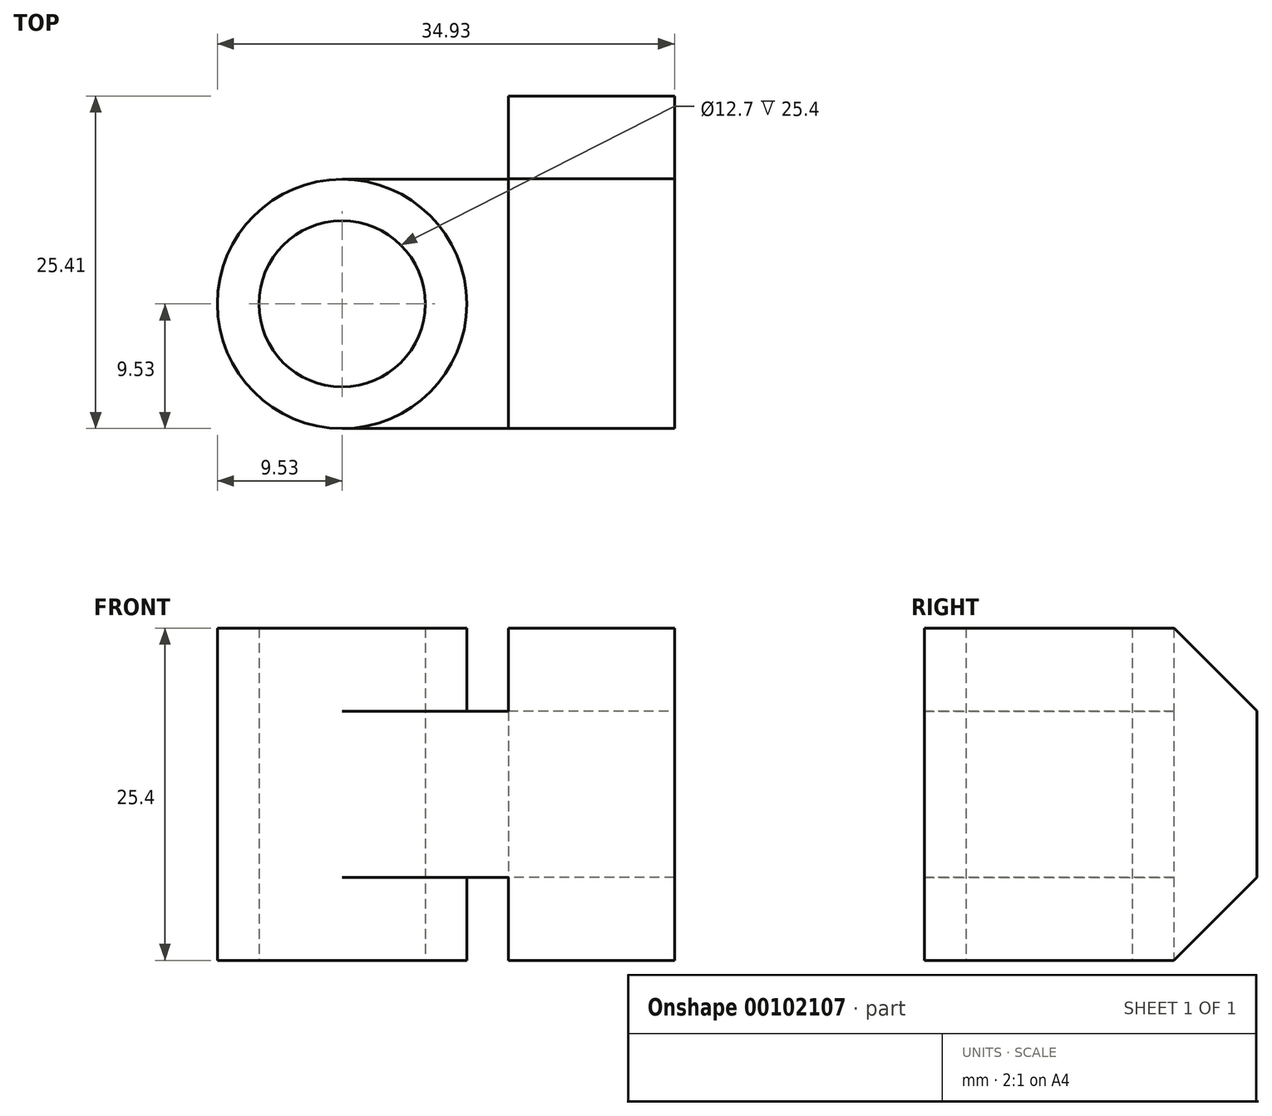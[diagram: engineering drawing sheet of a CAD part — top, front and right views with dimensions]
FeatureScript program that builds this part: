
annotation { "Feature Type Name" : "Feature", "Feature Type Description" : "" }
export const myFeature = defineFeature(function(context is Context, id is Id, definition is map)
    precondition{}
    {
        {
            var Q0;
            Q0=qCreatedBy(makeId("Top.planeOp"),FACE);
            var sketch = newSketch(context, id + "F0", { "sketchPlane" : qUnion([Q0])});
            skCircle(sketch, "E0", {"center": v(0, 0) * mm, "radius": 6.35 * mm});
            skCircle(sketch, "E1", {"center": v(0, 0) * mm, "radius": 9.53 * mm});
            skSolve(sketch);
        }
        {
            var Q0;
            Q0=qSketchRegion(id+"F0",true);
            extrude(context, id + "F1", {"entities" : qUnion([Q0]), "endBound" : BoundingType.SYMMETRIC, "depth" : 25.4 * mm});
        }
        {
            var Q0;
            Q0=qCreatedBy(makeId("Top.planeOp"),FACE);
            var sketch = newSketch(context, id + "F2", { "sketchPlane" : qUnion([Q0])});
            skLineSegment(sketch, "E2", {"start": v(0, -9.53) * mm, "end": v(12.7, -9.53) * mm});
            skLineSegment(sketch, "E3", {"start": v(0, 9.53) * mm, "end": v(12.7, 9.53) * mm});
            skArc(sketch, "E4", {"start": v(0, -9.53) * mm, "mid": v(9.53, 0) * mm, "end": v(0, 9.53) * mm});
            skLineSegment(sketch, "E5", {"start": v(12.7, 9.53) * mm, "end": v(12.7, -9.53) * mm});
            skSolve(sketch);
        }
        {
            var Q0;
            Q0=qSketchRegion(id+"F2",true);
            extrude(context, id + "F3", {"entities" : qUnion([Q0]), "operationType" : NewBodyOperationType.ADD, "endBound" : BoundingType.SYMMETRIC, "depth" : 12.7 * mm});
        }
        {
            var Q0;
            Q0=qCreatedBy(makeId("Top.planeOp"),FACE);
            var sketch = newSketch(context, id + "F4", { "sketchPlane" : qUnion([Q0])});
            skLineSegment(sketch, "E6", {"start": v(12.7, 0) * mm, "end": v(12.7, 15.88) * mm});
            skLineSegment(sketch, "E7", {"start": v(12.7, 15.88) * mm, "end": v(25.4, 15.88) * mm});
            skLineSegment(sketch, "E8", {"start": v(25.4, 15.88) * mm, "end": v(25.4, -9.52) * mm});
            skLineSegment(sketch, "E9", {"start": v(25.4, -9.53) * mm, "end": v(12.7, -9.53) * mm});
            skLineSegment(sketch, "E10", {"start": v(12.7, -9.53) * mm, "end": v(12.7, 0) * mm});
            skLineSegment(sketch, "E11", {"start": v(0, 9.53) * mm, "end": v(12.7, 9.53) * mm});
            skLineSegment(sketch, "E12", {"start": v(12.7, -9.53) * mm, "end": v(0, -9.53) * mm});
            skSolve(sketch);
        }
        {
            var Q0;
            Q0 = qSketchRegion(id + "F4", true);
            extrude(context, id + "F5", {"entities" : qUnion([Q0]), "operationType" : NewBodyOperationType.ADD, "endBound" : BoundingType.SYMMETRIC, "depth" : 25.4 * mm});
        }
        {
            var Q0;
            Q0=qCreatedBy(makeId("Right.planeOp"),FACE);
            var sketch = newSketch(context, id + "F6", { "sketchPlane" : qUnion([Q0])});
            skLineSegment(sketch, "E13", {"start": v(15.87, -6.35) * mm, "end": v(9.52, -12.7) * mm});
            skLineSegment(sketch, "E14", {"start": v(9.52, -12.7) * mm, "end": v(15.87, -12.7) * mm});
            skLineSegment(sketch, "E15", {"start": v(15.87, -12.7) * mm, "end": v(15.87, -6.35) * mm});
            skSolve(sketch);
        }
        {
            var Q0;
            Q0 = qSketchRegion(id + "F6", true);
            extrude(context, id + "F7", {"entities" : qUnion([Q0]), "operationType" : NewBodyOperationType.REMOVE, "endBound" : BoundingType.THROUGH_ALL, "depth" : 25.4 * mm});
        }
        {
            var Q0;
            Q0=qCreatedBy(makeId("Right.planeOp"),FACE);
            var sketch = newSketch(context, id + "F8", { "sketchPlane" : qUnion([Q0])});
            skLineSegment(sketch, "E16", {"start": v(9.56, 12.7) * mm, "end": v(15.9, 6.35) * mm});
            skLineSegment(sketch, "E17", {"start": v(15.9, 6.35) * mm, "end": v(15.9, 12.7) * mm});
            skLineSegment(sketch, "E18", {"start": v(15.9, 12.7) * mm, "end": v(9.56, 12.7) * mm});
            skSolve(sketch);
        }
        {
            var Q0;
            Q0 = qSketchRegion(id + "F8", true);
            extrude(context, id + "F9", {"entities" : qUnion([Q0]), "operationType" : NewBodyOperationType.REMOVE, "endBound" : BoundingType.THROUGH_ALL, "depth" : 25.4 * mm});
        }
    });
